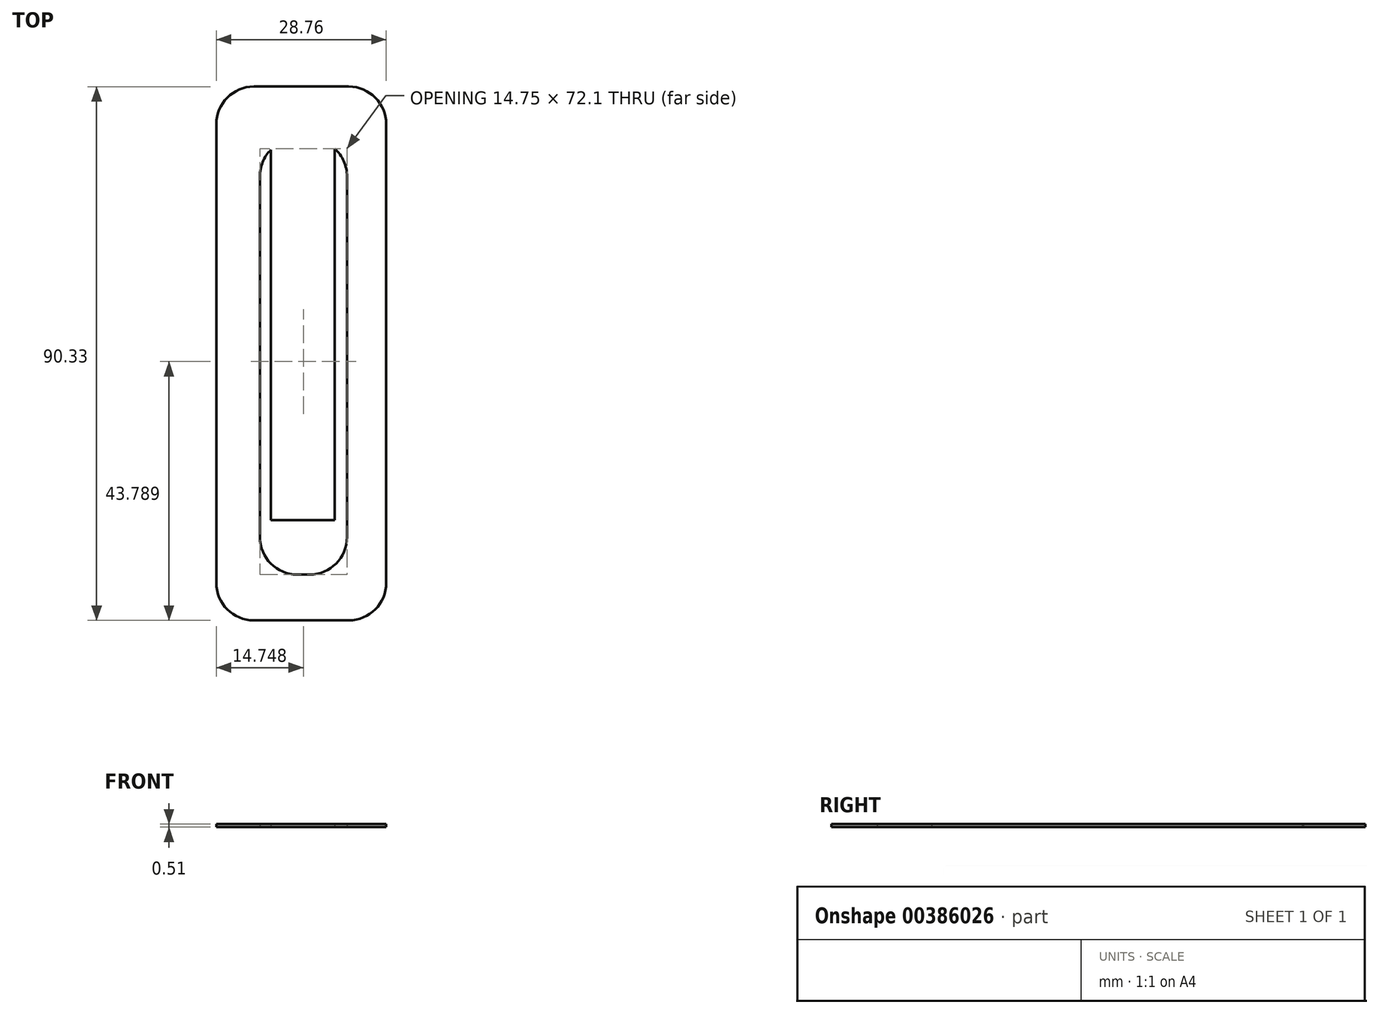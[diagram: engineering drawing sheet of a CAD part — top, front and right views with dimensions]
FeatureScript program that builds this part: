
annotation { "Feature Type Name" : "Feature", "Feature Type Description" : "" }
export const myFeature = defineFeature(function(context is Context, id is Id, definition is map)
    precondition{}
    {
        {
            var Q0;
            Q0=qCreatedBy(makeId("Top.planeOp"),FACE);
            var sketch = newSketch(context, id + "F0", { "sketchPlane" : qUnion([Q0])});
            skLineSegment(sketch, "E0.top", {"start": v(-1.95, -37.24) * mm, "end": v(0.1, -37.24) * mm});
            skLineSegment(sketch, "E0.left", {"start": v(-8.3, 30.15) * mm, "end": v(-8.3, -30.89) * mm});
            skLineSegment(sketch, "E0.right", {"start": v(6.45, 30.15) * mm, "end": v(6.45, -30.89) * mm});
            skLineSegment(sketch, "E1.bottom", {"start": v(-9.32, 45.35) * mm, "end": v(6.74, 45.35) * mm});
            skLineSegment(sketch, "E1.top", {"start": v(-9.32, -44.98) * mm, "end": v(6.74, -44.98) * mm});
            skLineSegment(sketch, "E1.left", {"start": v(-15.67, 39) * mm, "end": v(-15.67, -38.63) * mm});
            skLineSegment(sketch, "E1.right", {"start": v(13.09, 39) * mm, "end": v(13.09, -38.63) * mm});
            skPoint(sketch, "E2.visualSharp", {"position": v(-8.3, 36.5) * mm});
            skArc(sketch, "E2.filletArc", {"start": v(-6.44, 34.64) * mm, "mid": v(-7.81, 32.58) * mm, "end": v(-8.3, 30.15) * mm});
            skPoint(sketch, "E3.visualSharp", {"position": v(-8.3, -37.24) * mm});
            skArc(sketch, "E3.filletArc", {"start": v(-8.3, -30.89) * mm, "mid": v(-6.44, -35.38) * mm, "end": v(-1.95, -37.24) * mm});
            skPoint(sketch, "E4.visualSharp", {"position": v(6.45, 36.5) * mm});
            skArc(sketch, "E4.filletArc", {"start": v(6.45, 30.15) * mm, "mid": v(5.9, 32.73) * mm, "end": v(4.37, 34.86) * mm});
            skPoint(sketch, "E5.visualSharp", {"position": v(6.45, -37.24) * mm});
            skArc(sketch, "E5.filletArc", {"start": v(0.1, -37.24) * mm, "mid": v(4.6, -35.38) * mm, "end": v(6.45, -30.89) * mm});
            skPoint(sketch, "E6.visualSharp", {"position": v(13.09, 45.35) * mm});
            skArc(sketch, "E6.filletArc", {"start": v(13.09, 39) * mm, "mid": v(11.23, 43.5) * mm, "end": v(6.74, 45.35) * mm});
            skPoint(sketch, "E7.visualSharp", {"position": v(-15.67, 45.35) * mm});
            skArc(sketch, "E7.filletArc", {"start": v(-9.32, 45.35) * mm, "mid": v(-13.81, 43.5) * mm, "end": v(-15.67, 39) * mm});
            skPoint(sketch, "E8.visualSharp", {"position": v(13.09, -44.98) * mm});
            skArc(sketch, "E8.filletArc", {"start": v(6.74, -44.98) * mm, "mid": v(11.23, -43.12) * mm, "end": v(13.09, -38.63) * mm});
            skPoint(sketch, "E9.visualSharp", {"position": v(-15.67, -44.98) * mm});
            skArc(sketch, "E9.filletArc", {"start": v(-15.67, -38.63) * mm, "mid": v(-13.81, -43.12) * mm, "end": v(-9.32, -44.98) * mm});
            skLineSegment(sketch, "E10.top", {"start": v(-6.44, -28.02) * mm, "end": v(4.37, -28.02) * mm});
            skLineSegment(sketch, "E10.left", {"start": v(-6.44, 34.64) * mm, "end": v(-6.44, -28.02) * mm});
            skLineSegment(sketch, "E10.right", {"start": v(4.37, 34.64) * mm, "end": v(4.37, -28.02) * mm});
            skLineSegment(sketch, "E11.bottom", {"start": v(-6.44, 45.35) * mm, "end": v(4.37, 45.35) * mm});
            skLineSegment(sketch, "E11.left", {"start": v(-6.44, 34.64) * mm, "end": v(-6.44, 26.38) * mm});
            skLineSegment(sketch, "E11.right", {"start": v(4.37, 34.86) * mm, "end": v(4.37, 26.38) * mm});
            skPoint(sketch, "E12.center.orphan", {"position": v(-1.03, 45.35) * mm});
            skArc(sketch, "E13", {"start": v(4.37, 34.64) * mm, "mid": v(4.44, 34.68) * mm, "end": v(4.52, 34.72) * mm});
            skArc(sketch, "E14.trimOffspring", {"start": v(10.86, 43.83) * mm, "mid": v(-0.85, 57.34) * mm, "end": v(-12.97, 44.2) * mm});
            skCircle(sketch, "E15", {"center": v(-4.93, 52.85) * mm, "radius": 1.57 * mm});
            skCircle(sketch, "E16", {"center": v(3.24, 53.02) * mm, "radius": 1.63 * mm});
            skArc(sketch, "E17", {"start": v(-4.05, 49.02) * mm, "mid": v(-1.1, 45.8) * mm, "end": v(1.85, 49.02) * mm});
            skLineSegment(sketch, "E18", {"start": v(-4.05, 49.02) * mm, "end": v(1.85, 49.02) * mm});
            skSolve(sketch);
        }
        {
            var Q0;
            Q0=makeQuery(id+"F0.imprint","IMPRINT",FACE,{"disambiguationData":[TD([[makeQuery(id+"F0.imprint","IMPRINT",EDGE,{"derivedFrom":sQuery(id+"F0.wireOp",EDGE,"E0.top")}),-1.0]])]});
            var Q1;
            {var subQ6=sQuery(id+"F0.wireOp",EDGE,"E11.bottom");Q1=makeQuery(id+"F0.imprint","IMPRINT",FACE,{"disambiguationData":[TD([[makeQuery(id+"F0.imprint","IMPRINT",EDGE,{"derivedFrom":subQ6}),1.0]])]});}
            extrude(context, id + "F1", {"entities" : qUnion([Q0, Q1]), "depth" : 0.5 * mm});
        }
    });
